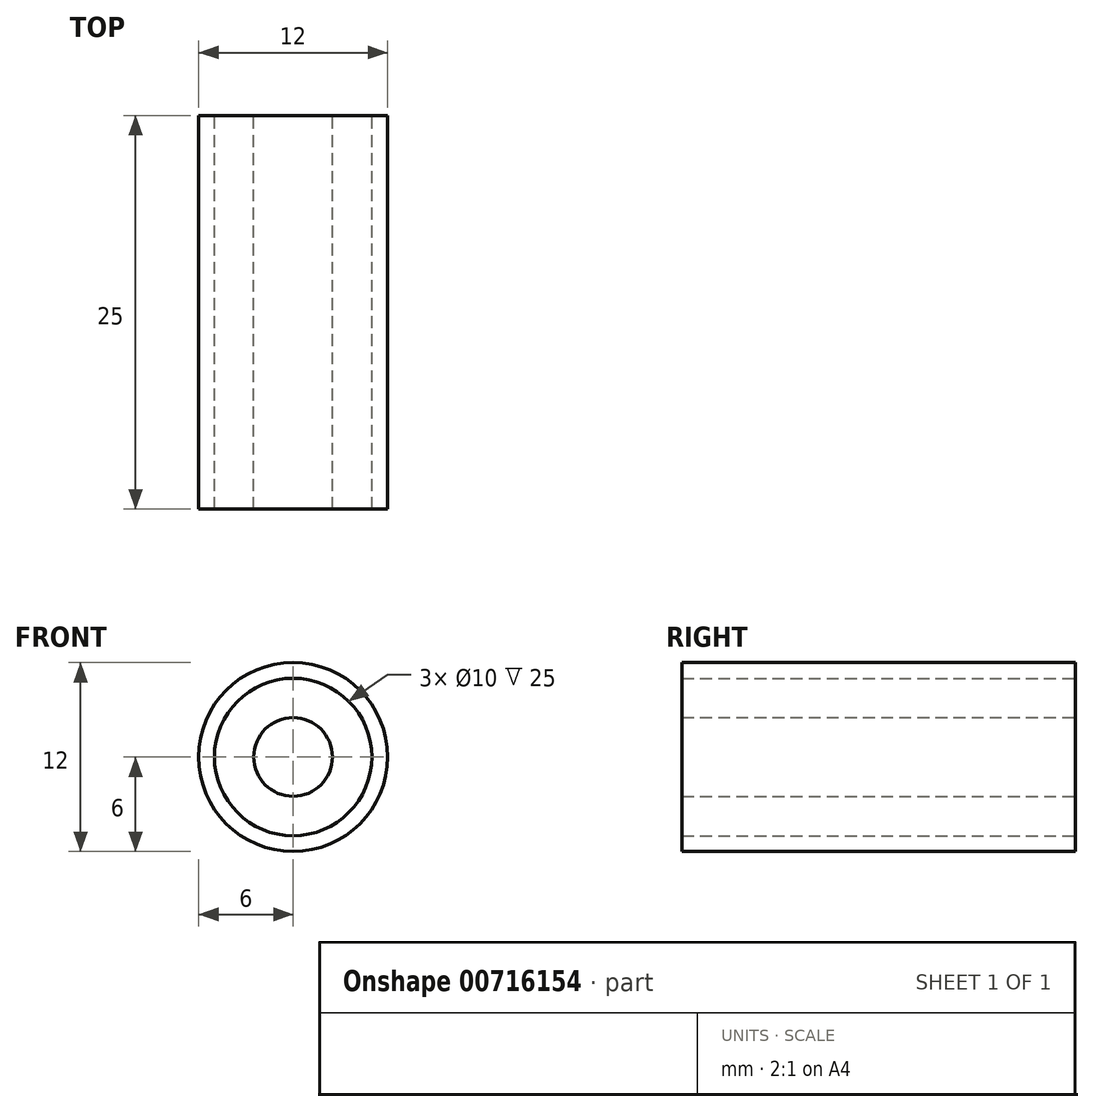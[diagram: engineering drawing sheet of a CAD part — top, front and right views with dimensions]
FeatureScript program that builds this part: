
annotation { "Feature Type Name" : "Feature", "Feature Type Description" : "" }
export const myFeature = defineFeature(function(context is Context, id is Id, definition is map)
    precondition{}
    {
        {
            var Q0;
            Q0=qCreatedBy(makeId("Front.planeOp"),FACE);
            var sketch = newSketch(context, id + "F0", { "sketchPlane" : qUnion([Q0])});
            skCircle(sketch, "E0", {"center": v(0, 0) * mm, "radius": 6 * mm});
            skCircle(sketch, "E1", {"center": v(0, 0) * mm, "radius": 5 * mm});
            skCircle(sketch, "E2", {"center": v(0, 0) * mm, "radius": 1.5 * mm});
            skSolve(sketch);
        }
        {
            var Q0;
            Q0 = qSketchRegion(id + "F0", true);
            extrude(context, id + "F1", {"entities" : qUnion([Q0]), "depth" : 25 * mm, "offsetDistance" : 25 * mm});
        }
        {
            var Q0;
            Q0 = qSketchRegion(id + "F0", true);
            var Q1;
            Q1=makeQuery(id+"F1.opExtrude","CAP_FACE",FACE,{"disambiguationData":[OSD([sQuery(id+"F0.wireOp",EDGE,"E0"),sQuery(id+"F0.wireOp",EDGE,"E1")])],"isStart":true});
            extrude(context, id + "F2", {"entities" : qUnion([Q0, Q1]), "depth" : 25 * mm, "offsetDistance" : 25 * mm});
        }
        {
            var Q0;
            Q0=qCreatedBy(makeId("Front.planeOp"),FACE);
            var sketch = newSketch(context, id + "F3", { "sketchPlane" : qUnion([Q0])});
            skCircle(sketch, "E3", {"center": v(0, 0) * mm, "radius": 2.5 * mm});
            skSolve(sketch);
        }
        {
            var Q0;
            Q0=makeQuery(id+"F3.imprint","IMPRINT",FACE,{"disambiguationData":[TD([[makeQuery(id+"F3.imprint","IMPRINT",EDGE,{"derivedFrom":sQuery(id+"F3.wireOp",EDGE,"E3")}),1.0]])]});
            extrude(context, id + "F4", {"entities" : qUnion([Q0]), "depth" : 25 * mm, "offsetDistance" : 25 * mm});
        }
    });
